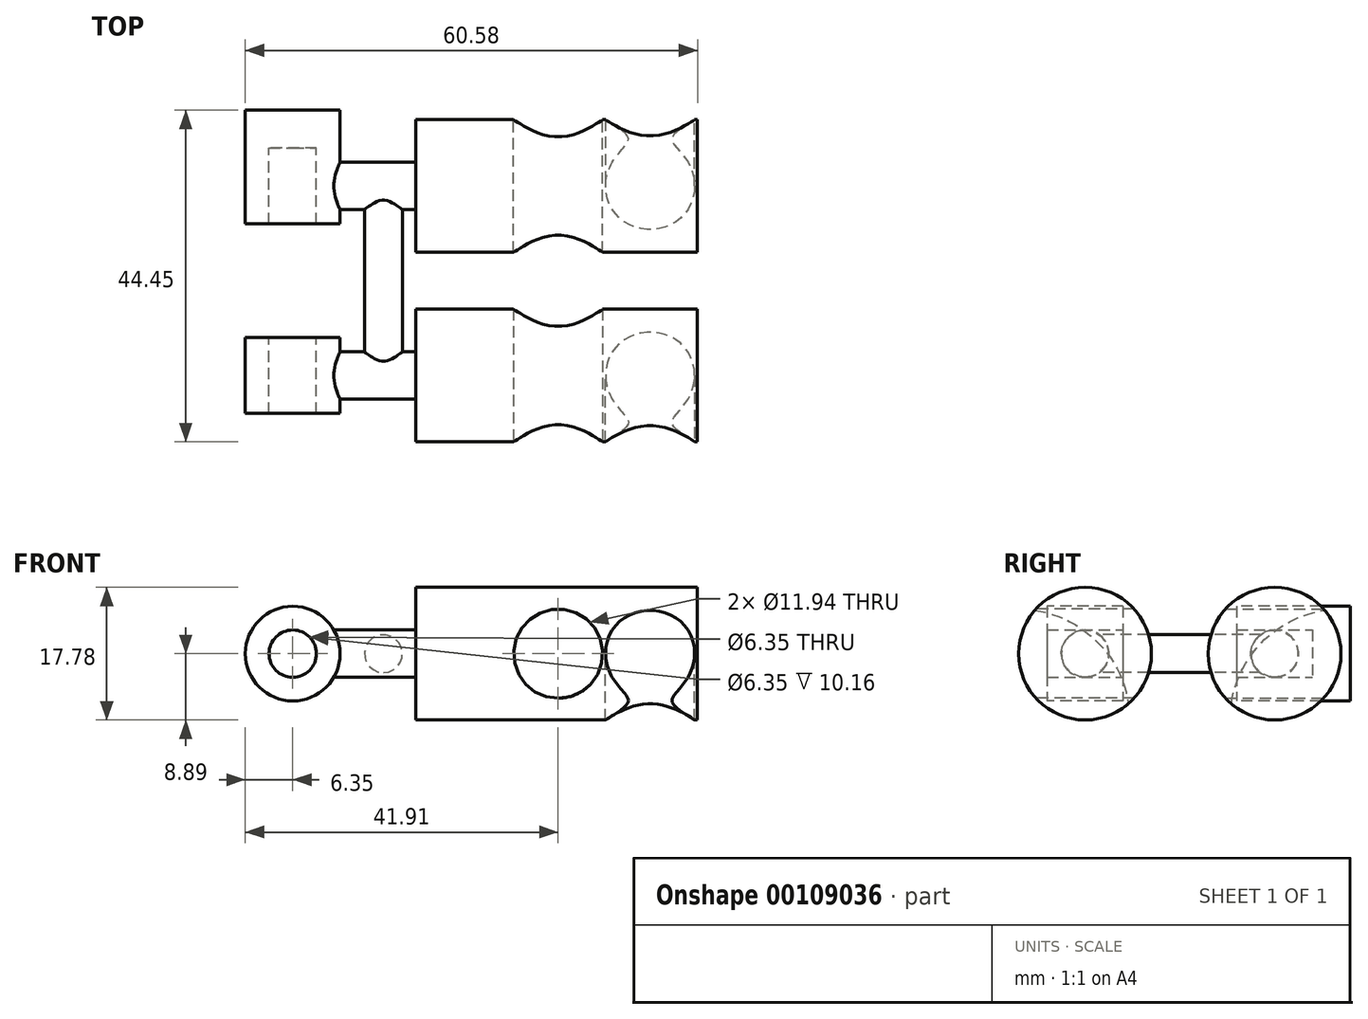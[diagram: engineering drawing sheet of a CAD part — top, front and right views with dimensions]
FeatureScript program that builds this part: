
annotation { "Feature Type Name" : "Feature", "Feature Type Description" : "" }
export const myFeature = defineFeature(function(context is Context, id is Id, definition is map)
    precondition{}
    {
        {
            var Q0;
            Q0=qCreatedBy(makeId("Right.planeOp"),FACE);
            var sketch = newSketch(context, id + "F0", { "sketchPlane" : qUnion([Q0])});
            skCircle(sketch, "E0", {"center": v(0, 0) * mm, "radius": 8.9 * mm});
            skSolve(sketch);
        }
        {
            var Q0;
            Q0=makeQuery(id+"F0.imprint","IMPRINT",FACE,{"disambiguationData":[TD([[makeQuery(id+"F0.imprint","IMPRINT",EDGE,{"derivedFrom":sQuery(id+"F0.wireOp",EDGE,"E0")}),1.0]])]});
            extrude(context, id + "F1", {"entities" : qUnion([Q0]), "depth" : 35.56 * mm, "hasSecondDirection" : true, "secondDirectionOppositeDirection" : true, "secondDirectionDepth" : 12.7 * mm});
        }
        {
            var Q0;
            Q0=qCreatedBy(makeId("Right.planeOp"),FACE);
            var sketch = newSketch(context, id + "F2", { "sketchPlane" : qUnion([Q0])});
            skLineSegment(sketch, "E1", {"start": v(-25.4, 0) * mm, "end": v(-8.9, 0) * mm});
            skLineSegment(sketch, "E2", {"start": v(0, -8.9) * mm, "end": v(0, -14.21) * mm});
            skArc(sketch, "E3", {"start": v(0, -8.9) * mm, "mid": v(-2.6, -2.6) * mm, "end": v(-8.9, 0) * mm});
            skSolve(sketch);
        }
        {
            var Q0;
            Q0=qCreatedBy(makeId("Top.planeOp"),FACE);
            var sketch = newSketch(context, id + "F3", { "sketchPlane" : qUnion([Q0])});
            skLineSegment(sketch, "E4", {"start": v(35.56, 0) * mm, "end": v(29.46, 0) * mm});
            skSolve(sketch);
        }
        {
            var Q0;
            Q0=qCreatedBy(makeId("Top.planeOp"),FACE);
            var sketch = newSketch(context, id + "F4", { "sketchPlane" : qUnion([Q0])});
            skLineSegment(sketch, "E5", {"start": v(6.35, 0) * mm, "end": v(6.35, 17.43) * mm});
            skLineSegment(sketch, "E6", {"start": v(6.35, 0) * mm, "end": v(6.35, -16.9) * mm});
            skLineSegment(sketch, "E7", {"start": v(0, 0) * mm, "end": v(6.35, 0) * mm});
            skLineSegment(sketch, "E8", {"start": v(0, 0) * mm, "end": v(29.46, 0) * mm});
            skSolve(sketch);
        }
        {
            var Q0;
            Q0=qCreatedBy(makeId("Front.planeOp"),FACE);
            var sketch = newSketch(context, id + "F5", { "sketchPlane" : qUnion([Q0])});
            skCircle(sketch, "E9", {"center": v(6.35, 0) * mm, "radius": 5.97 * mm});
            skSolve(sketch);
        }
        {
            var Q0;
            Q0=makeQuery(id+"F5.imprint","IMPRINT",FACE,{"disambiguationData":[TD([[makeQuery(id+"F5.imprint","IMPRINT",EDGE,{"derivedFrom":sQuery(id+"F5.wireOp",EDGE,"E9")}),1.0]])]});
            extrude(context, id + "F6", {"entities" : qUnion([Q0]), "operationType" : NewBodyOperationType.REMOVE, "oppositeDirection" : true, "depth" : 25.4 * mm, "hasSecondDirection" : true, "secondDirectionOppositeDirection" : false, "secondDirectionDepth" : 25.4 * mm});
        }
        {
            var Q0;
            Q0=qCreatedBy(makeId("Front.planeOp"),FACE);
            var sketch = newSketch(context, id + "F7", { "sketchPlane" : qUnion([Q0])});
            skLineSegment(sketch, "E10", {"start": v(6.35, 0) * mm, "end": v(18.67, 0) * mm});
            skSolve(sketch);
        }
        {
            var Q0;
            Q0=qCreatedBy(makeId("Front.planeOp"),FACE);
            cPlane(context, id + "F8", {"entities" : qUnion([Q0]), "cplaneType" : CPlaneType.OFFSET, "offset" : 25.4 * mm, "width" : 152.4 * mm, "height" : 152.4 * mm});
        }
        {
            var Q0;
            Q0=qCreatedBy(id+"F8.planeOp",FACE);
            var sketch = newSketch(context, id + "F9", { "sketchPlane" : qUnion([Q0])});
            skCircle(sketch, "E11", {"center": v(18.67, 0) * mm, "radius": 5.97 * mm});
            skLineSegment(sketch, "E12", {"start": v(24.64, 0) * mm, "end": v(25.02, 0) * mm});
            skLineSegment(sketch, "E13", {"start": v(25.02, 0) * mm, "end": v(35.56, 0) * mm});
            skLineSegment(sketch, "E14", {"start": v(12.32, 0) * mm, "end": v(12.7, 0) * mm});
            skSolve(sketch);
        }
        {
            var Q0;
            Q0=makeQuery(id+"F9.imprint","IMPRINT",FACE,{"disambiguationData":[TD([[makeQuery(id+"F9.imprint","IMPRINT",EDGE,{"derivedFrom":sQuery(id+"F9.wireOp",EDGE,"E11")}),1.0]])]});
            var Q1;
            Q1=sQuery(id+"F2.wireOp",EDGE,"E1");
            var Q2;
            Q2=sQuery(id+"F2.wireOp",EDGE,"E3");
            var Q3;
            Q3=sQuery(id+"F2.wireOp",EDGE,"E2");
            sweep(context, id + "F10", {"operationType" : NewBodyOperationType.REMOVE, "profiles" : qUnion([Q0]), "path" : qUnion([Q1, Q2, Q3])});
        }
        {
            var Q0;
            Q0=makeQuery(id+"F1.opExtrude","CAP_FACE",FACE,{"disambiguationData":[OSD([sQuery(id+"F0.wireOp",EDGE,"E0")])],"isStart":false});
            var Q1;
            Q1=sQuery(id+"F9.wireOp",EDGE,"E13");
            sweep(context, id + "F11", {"operationType" : NewBodyOperationType.REMOVE, "profiles" : qUnion([Q0]), "path" : qUnion([Q1])});
        }
        {
            var Q0;
            Q0=qCreatedBy(makeId("Front.planeOp"),FACE);
            cPlane(context, id + "F12", {"entities" : qUnion([Q0]), "cplaneType" : CPlaneType.OFFSET, "offset" : 12.7 * mm, "oppositeDirection" : true, "width" : 152.4 * mm, "height" : 152.4 * mm});
        }
        {
            var Q0;
            Q0=makeQuery(id+"F1.opExtrude","SWEPT_BODY",BODY,{"disambiguationData":[OSD([sQuery(id+"F0.wireOp",EDGE,"E0")])]});
            var Q1;
            Q1=qCreatedBy(id+"F12.planeOp",FACE);
            mirror(context, id + "F13", {"entities" : qUnion([Q0]), "mirrorPlane" : qUnion([Q1])});
        }
        {
            var Q0;
            Q0=qCreatedBy(makeId("Top.planeOp"),FACE);
            var sketch = newSketch(context, id + "F14", { "sketchPlane" : qUnion([Q0])});
            skLineSegment(sketch, "E15", {"start": v(25.02, 0) * mm, "end": v(34.29, 0) * mm});
            skLineSegment(sketch, "E16", {"start": v(25.02, 0) * mm, "end": v(25.02, 25.4) * mm});
            skArc(sketch, "E17", {"start": v(34.29, 0) * mm, "mid": v(38.78, 1.86) * mm, "end": v(40.64, 6.35) * mm});
            skLineSegment(sketch, "E18", {"start": v(40.64, 6.35) * mm, "end": v(40.64, 19.05) * mm});
            skArc(sketch, "E19", {"start": v(40.64, 19.05) * mm, "mid": v(38.78, 23.54) * mm, "end": v(34.29, 25.4) * mm});
            skLineSegment(sketch, "E20", {"start": v(25.02, 25.4) * mm, "end": v(34.29, 25.4) * mm});
            skLineSegment(sketch, "E21", {"start": v(-29.21, 25.4) * mm, "end": v(-12.7, 25.4) * mm});
            skLineSegment(sketch, "E22", {"start": v(-29.21, 0) * mm, "end": v(-12.7, 0) * mm});
            skLineSegment(sketch, "E23", {"start": v(-12.7, 0) * mm, "end": v(-12.7, 25.4) * mm});
            skSolve(sketch);
        }
        {
            var Q0;
            Q0=makeQuery(id+"F1.opExtrude","CAP_FACE",FACE,{"disambiguationData":[OSD([sQuery(id+"F0.wireOp",EDGE,"E0")])],"isStart":true});
            var sketch = newSketch(context, id + "F15", { "sketchPlane" : qUnion([Q0])});
            skCircle(sketch, "E24", {"center": v(0, 0) * mm, "radius": 3.18 * mm});
            skSolve(sketch);
        }
        {
            var Q0;
            Q0=sQuery(id+"F14.wireOp",EDGE,"E22");
            cPlane(context, id + "F16", {"entities" : qUnion([Q0]), "cplaneType" : CPlaneType.LINE_ANGLE, "offset" : 25.4 * mm, "angle" : 0 * degree, "width" : 152.4 * mm, "height" : 152.4 * mm});
        }
        {
            var Q0;
            Q0=qCreatedBy(id+"F16.planeOp",FACE);
            var sketch = newSketch(context, id + "F17", { "sketchPlane" : qUnion([Q0])});
            skCircle(sketch, "E25", {"center": v(17.07, 0) * mm, "radius": 2.54 * mm});
            skCircle(sketch, "E26", {"center": v(29.21, 0) * mm, "radius": 3.18 * mm});
            skCircle(sketch, "E27", {"center": v(29.21, 0) * mm, "radius": 6.35 * mm});
            skSolve(sketch);
        }
        {
            var Q0;
            Q0=sQuery(id+"F14.wireOp",EDGE,"E21");
            cPlane(context, id + "F18", {"entities" : qUnion([Q0]), "cplaneType" : CPlaneType.LINE_ANGLE, "offset" : 25.4 * mm, "angle" : 0 * degree, "width" : 152.4 * mm, "height" : 152.4 * mm});
        }
        {
            var Q0;
            Q0=qCreatedBy(id+"F18.planeOp",FACE);
            var sketch = newSketch(context, id + "F19", { "sketchPlane" : qUnion([Q0])});
            skCircle(sketch, "E28", {"center": v(29.21, 0) * mm, "radius": 3.18 * mm});
            skCircle(sketch, "E29", {"center": v(29.21, 0) * mm, "radius": 6.35 * mm});
            skSolve(sketch);
        }
        {
            var Q0;
            Q0=makeQuery(id+"F13.opPattern","COPY",FACE,{"derivedFrom":makeQuery(id+"F1.opExtrude","CAP_FACE",FACE,{"disambiguationData":[OSD([sQuery(id+"F0.wireOp",EDGE,"E0")])],"isStart":true}),"instanceName":"1"});
            var sketch = newSketch(context, id + "F20", { "sketchPlane" : qUnion([Q0])});
            skCircle(sketch, "E30", {"center": v(-25.4, 0) * mm, "radius": 3.18 * mm});
            skSolve(sketch);
        }
        {
            var Q0;
            Q0=makeQuery(id+"F15.imprint","IMPRINT",FACE,{"disambiguationData":[TD([[makeQuery(id+"F15.imprint","IMPRINT",EDGE,{"derivedFrom":sQuery(id+"F15.wireOp",EDGE,"E24")}),1.0]])]});
            var Q1;
            Q1=sQuery(id+"F15.wireOp",EDGE,"E24");
            extrude(context, id + "F21", {"entities" : qUnion([Q0]), "operationType" : NewBodyOperationType.ADD, "surfaceEntities" : qUnion([Q1]), "depth" : 16.5 * mm});
        }
        {
            var Q0;
            Q0=makeQuery(id+"F20.imprint","IMPRINT",FACE,{"disambiguationData":[TD([[makeQuery(id+"F20.imprint","IMPRINT",EDGE,{"derivedFrom":sQuery(id+"F20.wireOp",EDGE,"E30")}),1.0]])]});
            extrude(context, id + "F22", {"entities" : qUnion([Q0]), "operationType" : NewBodyOperationType.ADD, "depth" : 16.5 * mm});
        }
        {
            var Q0;
            Q0=makeQuery(id+"F19.imprint","IMPRINT",FACE,{"disambiguationData":[TD([[makeQuery(id+"F19.imprint","IMPRINT",EDGE,{"derivedFrom":sQuery(id+"F19.wireOp",EDGE,"E28")}),1.0]])]});
            extrude(context, id + "F23", {"entities" : qUnion([Q0]), "operationType" : NewBodyOperationType.REMOVE, "oppositeDirection" : true, "depth" : 34.18 * mm, "hasSecondDirection" : true, "secondDirectionOppositeDirection" : false, "secondDirectionDepth" : 25.4 * mm});
        }
        {
            var Q0;
            Q0=makeQuery(id+"F17.imprint","IMPRINT",FACE,{"disambiguationData":[TD([[makeQuery(id+"F17.imprint","IMPRINT",EDGE,{"derivedFrom":sQuery(id+"F17.wireOp",EDGE,"E25")}),1.0]])]});
            extrude(context, id + "F24", {"entities" : qUnion([Q0]), "operationType" : NewBodyOperationType.ADD, "depth" : 25.4 * mm});
        }
        {
            var Q0;
            Q0=makeQuery(id+"F17.imprint","IMPRINT",FACE,{"disambiguationData":[TD([[makeQuery(id+"F17.imprint","IMPRINT",EDGE,{"derivedFrom":sQuery(id+"F17.wireOp",EDGE,"E26")}),-1.0]])]});
            var Q1;
            Q1=makeQuery(id+"F19.imprint","IMPRINT",FACE,{"disambiguationData":[TD([[makeQuery(id+"F19.imprint","IMPRINT",EDGE,{"derivedFrom":sQuery(id+"F19.wireOp",EDGE,"E28")}),-1.0]])]});
            extrude(context, id + "F25", {"entities" : qUnion([Q0, Q1]), "operationType" : NewBodyOperationType.ADD, "depth" : 5.08 * mm, "hasSecondDirection" : true, "secondDirectionOppositeDirection" : true, "secondDirectionDepth" : 5.08 * mm});
        }
        {
            var Q0;
            Q0=makeQuery(id+"F25.opExtrude","CAP_FACE",FACE,{"disambiguationData":[OSD([sQuery(id+"F19.wireOp",EDGE,"E28"),sQuery(id+"F19.wireOp",EDGE,"E29")])],"isStart":false});
            var sketch = newSketch(context, id + "F26", { "sketchPlane" : qUnion([Q0])});
            skCircle(sketch, "E31", {"center": v(29.21, 0) * mm, "radius": 6.35 * mm});
            skSolve(sketch);
        }
        {
            var Q0;
            Q0=makeQuery(id+"F26.imprint","IMPRINT",FACE,{"disambiguationData":[TD([[makeQuery(id+"F26.imprint","IMPRINT",EDGE,{"derivedFrom":sQuery(id+"F26.wireOp",EDGE,"E31")}),1.0]])]});
            var Q1;
            Q1=makeQuery(id+"F26.imprint","IMPRINT",FACE,{"disambiguationData":[TD([[makeQuery(id+"F26.imprint","IMPRINT",EDGE,{"derivedFrom":makeQuery(id+"F25.opExtrude","CAP_EDGE",EDGE,{"disambiguationData":[OSD([sQuery(id+"F19.wireOp",EDGE,"E28")])],"isStart":false})}),1.0]])]});
            extrude(context, id + "F27", {"entities" : qUnion([Q0, Q1]), "operationType" : NewBodyOperationType.ADD, "depth" : 5.08 * mm});
        }
    });
